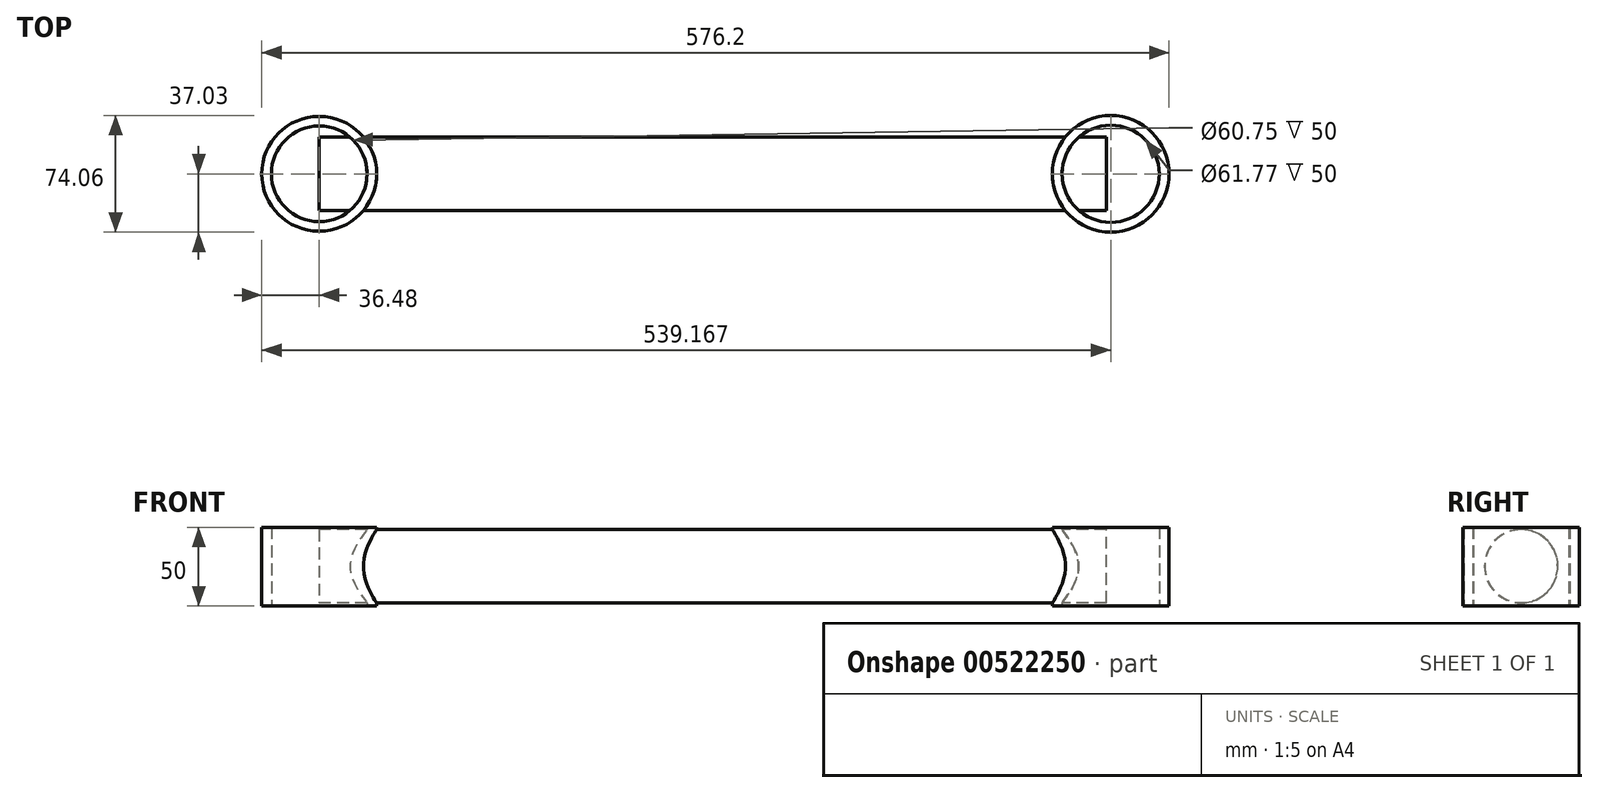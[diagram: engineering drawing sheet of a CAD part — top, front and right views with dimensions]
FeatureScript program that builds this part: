
annotation { "Feature Type Name" : "Feature", "Feature Type Description" : "" }
export const myFeature = defineFeature(function(context is Context, id is Id, definition is map)
    precondition{}
    {
        {
            var Q0;
            Q0=qCreatedBy(makeId("Top.planeOp"),FACE);
            var sketch = newSketch(context, id + "F0", { "sketchPlane" : qUnion([Q0])});
            skCircle(sketch, "E0", {"center": v(0, 0) * mm, "radius": 36.48 * mm});
            skCircle(sketch, "E1", {"center": v(0, 0) * mm, "radius": 30.38 * mm});
            skSolve(sketch);
        }
        {
            var Q0;
            Q0=makeQuery(id+"F0.imprint","IMPRINT",FACE,{"disambiguationData":[TD([[makeQuery(id+"F0.imprint","IMPRINT",EDGE,{"derivedFrom":sQuery(id+"F0.wireOp",EDGE,"E0")}),1.0]])]});
            extrude(context, id + "F1", {"entities" : qUnion([Q0]), "depth" : 50 * mm, "offsetDistance" : 25 * mm});
        }
        {
            var Q0;
            Q0=qCreatedBy(makeId("Right.planeOp"),FACE);
            var sketch = newSketch(context, id + "F2", { "sketchPlane" : qUnion([Q0])});
            skCircle(sketch, "E2", {"center": v(0, 25.27) * mm, "radius": 23.3 * mm});
            skSolve(sketch);
        }
        {
            var Q0;
            Q0 = qSketchRegion(id + "F2", true);
            extrude(context, id + "F3", {"entities" : qUnion([Q0]), "operationType" : NewBodyOperationType.ADD, "depth" : 500 * mm, "offsetDistance" : 25 * mm});
        }
        {
            var Q0;
            Q0=qCreatedBy(makeId("Top.planeOp"),FACE);
            var sketch = newSketch(context, id + "F4", { "sketchPlane" : qUnion([Q0])});
            skCircle(sketch, "E3", {"center": v(502.69, 0) * mm, "radius": 37.03 * mm});
            skCircle(sketch, "E4", {"center": v(502.69, 0) * mm, "radius": 30.89 * mm});
            skSolve(sketch);
        }
        {
            var Q0;
            Q0=makeQuery(id+"F4.imprint","IMPRINT",FACE,{"disambiguationData":[TD([[makeQuery(id+"F4.imprint","IMPRINT",EDGE,{"derivedFrom":sQuery(id+"F4.wireOp",EDGE,"E3")}),1.0]])]});
            extrude(context, id + "F5", {"entities" : qUnion([Q0]), "operationType" : NewBodyOperationType.ADD, "depth" : 50 * mm, "offsetDistance" : 25 * mm});
        }
    });
